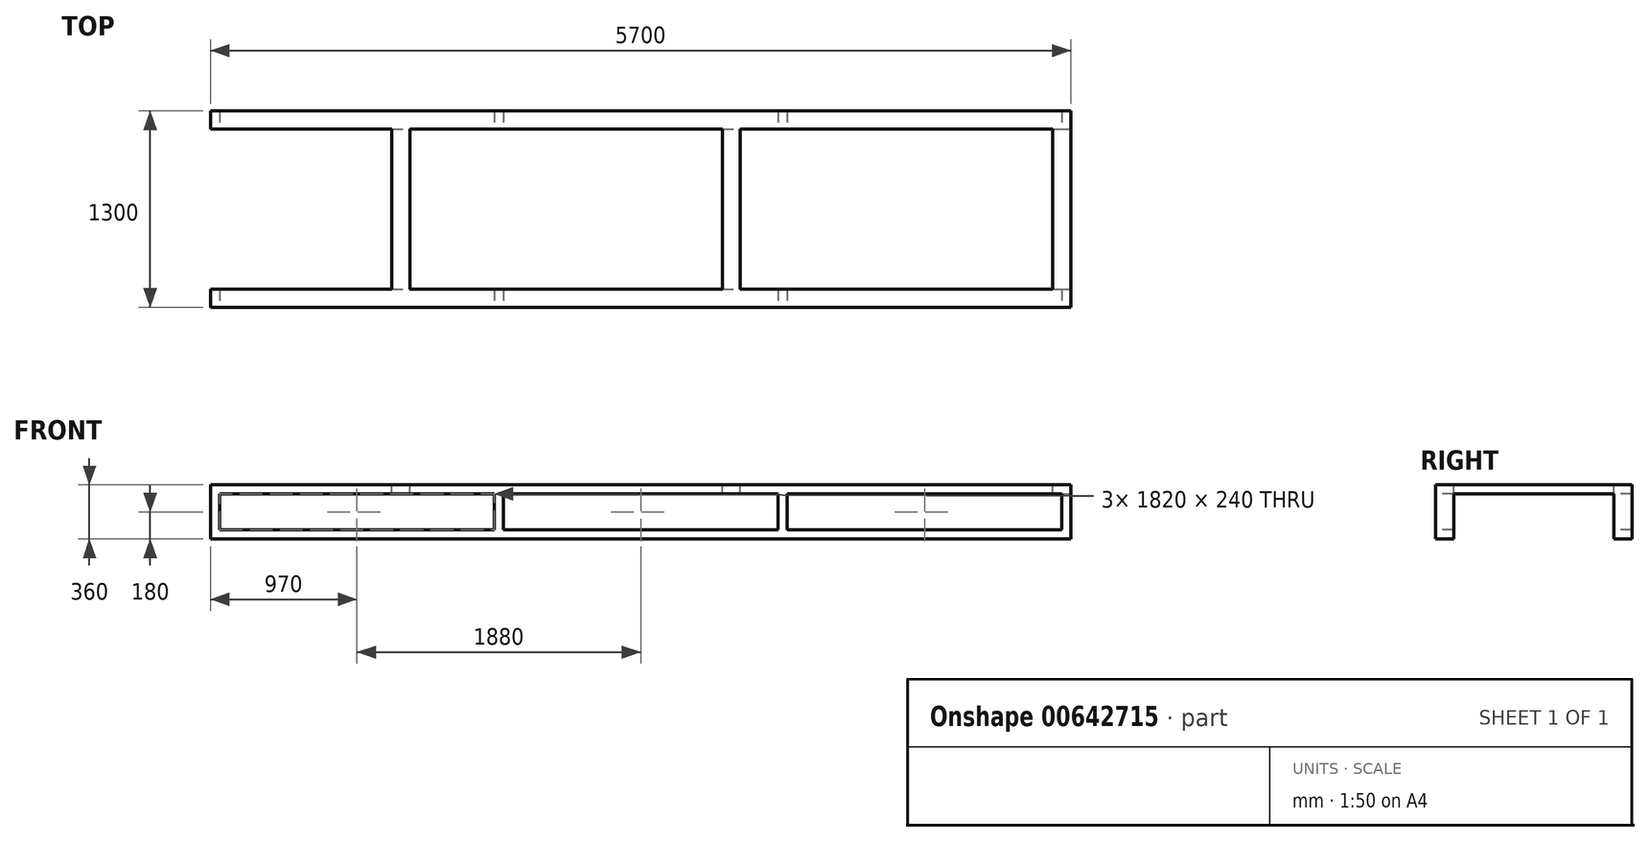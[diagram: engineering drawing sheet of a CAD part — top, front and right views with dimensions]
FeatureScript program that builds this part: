
annotation { "Feature Type Name" : "Feature", "Feature Type Description" : "" }
export const myFeature = defineFeature(function(context is Context, id is Id, definition is map)
    precondition{}
    {
        {
            var Q0;
            Q0=qCreatedBy(makeId("Top.planeOp"),FACE);
            var sketch = newSketch(context, id + "F0", { "sketchPlane" : qUnion([Q0])});
            skLineSegment(sketch, "E0.bottom", {"start": v(0, 0) * mm, "end": v(5700, 0) * mm});
            skLineSegment(sketch, "E0.top", {"start": v(0, 120) * mm, "end": v(5700, 120) * mm});
            skLineSegment(sketch, "E0.left", {"start": v(0, 0) * mm, "end": v(0, 120) * mm});
            skLineSegment(sketch, "E0.right", {"start": v(5700, 0) * mm, "end": v(5700, 120) * mm});
            skLineSegment(sketch, "E1.bottom", {"start": v(0, 1300) * mm, "end": v(5700, 1300) * mm});
            skLineSegment(sketch, "E1.top", {"start": v(0, 1180) * mm, "end": v(5700, 1180) * mm});
            skLineSegment(sketch, "E1.left", {"start": v(0, 1300) * mm, "end": v(0, 1180) * mm});
            skLineSegment(sketch, "E1.right", {"start": v(5700, 1300) * mm, "end": v(5700, 1180) * mm});
            skLineSegment(sketch, "E2.bottom", {"start": v(5700, 1180) * mm, "end": v(5580, 1180) * mm});
            skLineSegment(sketch, "E2.top", {"start": v(5700, 120) * mm, "end": v(5580, 120) * mm});
            skLineSegment(sketch, "E2.left", {"start": v(5700, 1180) * mm, "end": v(5700, 120) * mm});
            skLineSegment(sketch, "E2.right", {"start": v(5580, 1180) * mm, "end": v(5580, 120) * mm});
            skLineSegment(sketch, "E3.bottom", {"start": v(1200, 1180) * mm, "end": v(1320, 1180) * mm});
            skLineSegment(sketch, "E3.top", {"start": v(1200, 120) * mm, "end": v(1320, 120) * mm});
            skLineSegment(sketch, "E3.left", {"start": v(1200, 1180) * mm, "end": v(1200, 120) * mm});
            skLineSegment(sketch, "E3.right", {"start": v(1320, 1180) * mm, "end": v(1320, 120) * mm});
            skLineSegment(sketch, "E4.bottom", {"start": v(3390, 1180) * mm, "end": v(3510, 1180) * mm});
            skLineSegment(sketch, "E4.top", {"start": v(3390, 120) * mm, "end": v(3510, 120) * mm});
            skLineSegment(sketch, "E4.left", {"start": v(3390, 1180) * mm, "end": v(3390, 120) * mm});
            skLineSegment(sketch, "E4.right", {"start": v(3510, 1180) * mm, "end": v(3510, 120) * mm});
            skSolve(sketch);
        }
        {
            var Q0;
            Q0=makeQuery(id+"F0.imprint","IMPRINT",FACE,{"disambiguationData":[TD([[makeQuery(id+"F0.imprint","IMPRINT",EDGE,{"derivedFrom":sQuery(id+"F0.wireOp",EDGE,"E1.bottom")}),-1.0]])]});
            var Q1;
            Q1=makeQuery(id+"F0.imprint","IMPRINT",FACE,{"disambiguationData":[TD([[makeQuery(id+"F0.imprint","IMPRINT",EDGE,{"derivedFrom":sQuery(id+"F0.wireOp",EDGE,"E0.bottom")}),1.0]])]});
            var Q2;
            Q2=makeQuery(id+"F0.imprint","IMPRINT",FACE,{"disambiguationData":[TD([[makeQuery(id+"F0.imprint","IMPRINT",EDGE,{"derivedFrom":sQuery(id+"F0.wireOp",EDGE,"E3.bottom")}),-1.0]])]});
            var Q3;
            Q3=makeQuery(id+"F0.imprint","IMPRINT",FACE,{"disambiguationData":[TD([[makeQuery(id+"F0.imprint","IMPRINT",EDGE,{"derivedFrom":sQuery(id+"F0.wireOp",EDGE,"E4.bottom")}),-1.0]])]});
            var Q4;
            Q4=makeQuery(id+"F0.imprint","IMPRINT",FACE,{"disambiguationData":[TD([[makeQuery(id+"F0.imprint","IMPRINT",EDGE,{"derivedFrom":sQuery(id+"F0.wireOp",EDGE,"E2.bottom")}),1.0]])]});
            extrude(context, id + "F1", {"entities" : qUnion([Q0, Q1, Q2, Q3, Q4]), "depth" : 60 * mm, "offsetDistance" : 25 * mm});
        }
        {
            var Q0;
            Q0=makeQuery(id+"F1.opExtrude","CAP_FACE",FACE,{"disambiguationData":[OSD([sQuery(id+"F0.wireOp",EDGE,"E0.bottom"),sQuery(id+"F0.wireOp",EDGE,"E0.top"),sQuery(id+"F0.wireOp",EDGE,"E0.left"),sQuery(id+"F0.wireOp",EDGE,"E0.right"),sQuery(id+"F0.wireOp",EDGE,"E1.bottom"),sQuery(id+"F0.wireOp",EDGE,"E1.top"),sQuery(id+"F0.wireOp",EDGE,"E1.left"),sQuery(id+"F0.wireOp",EDGE,"E1.right"),sQuery(id+"F0.wireOp",EDGE,"E2.left"),sQuery(id+"F0.wireOp",EDGE,"E2.right"),sQuery(id+"F0.wireOp",EDGE,"E3.left"),sQuery(id+"F0.wireOp",EDGE,"E3.right"),sQuery(id+"F0.wireOp",EDGE,"E4.left"),sQuery(id+"F0.wireOp",EDGE,"E4.right")])],"isStart":false});
            var sketch = newSketch(context, id + "F2", { "sketchPlane" : qUnion([Q0])});
            skLineSegment(sketch, "E5.bottom", {"start": v(0, 1300) * mm, "end": v(60, 1300) * mm});
            skLineSegment(sketch, "E5.top", {"start": v(0, 1180) * mm, "end": v(60, 1180) * mm});
            skLineSegment(sketch, "E5.left", {"start": v(0, 1300) * mm, "end": v(0, 1180) * mm});
            skLineSegment(sketch, "E5.right", {"start": v(60, 1300) * mm, "end": v(60, 1180) * mm});
            skLineSegment(sketch, "E6.0.1.0", {"start": v(60, 120) * mm, "end": v(60, 0) * mm});
            skLineSegment(sketch, "E6.0.1.1", {"start": v(0, 0) * mm, "end": v(60, 0) * mm});
            skLineSegment(sketch, "E6.0.1.2", {"start": v(0, 120) * mm, "end": v(0, 0) * mm});
            skLineSegment(sketch, "E6.0.1.3", {"start": v(0, 120) * mm, "end": v(60, 120) * mm});
            skLineSegment(sketch, "E6.1.0.0", {"start": v(1940, 1300) * mm, "end": v(1940, 1180) * mm});
            skLineSegment(sketch, "E6.1.0.1", {"start": v(1880, 1180) * mm, "end": v(1940, 1180) * mm});
            skLineSegment(sketch, "E6.1.0.2", {"start": v(1880, 1300) * mm, "end": v(1880, 1180) * mm});
            skLineSegment(sketch, "E6.1.0.3", {"start": v(1880, 1300) * mm, "end": v(1940, 1300) * mm});
            skLineSegment(sketch, "E6.1.1.0", {"start": v(1940, 120) * mm, "end": v(1940, 0) * mm});
            skLineSegment(sketch, "E6.1.1.1", {"start": v(1880, 0) * mm, "end": v(1940, 0) * mm});
            skLineSegment(sketch, "E6.1.1.2", {"start": v(1880, 120) * mm, "end": v(1880, 0) * mm});
            skLineSegment(sketch, "E6.1.1.3", {"start": v(1880, 120) * mm, "end": v(1940, 120) * mm});
            skLineSegment(sketch, "E6.2.0.0", {"start": v(3820, 1300) * mm, "end": v(3820, 1180) * mm});
            skLineSegment(sketch, "E6.2.0.1", {"start": v(3760, 1180) * mm, "end": v(3820, 1180) * mm});
            skLineSegment(sketch, "E6.2.0.2", {"start": v(3760, 1300) * mm, "end": v(3760, 1180) * mm});
            skLineSegment(sketch, "E6.2.0.3", {"start": v(3760, 1300) * mm, "end": v(3820, 1300) * mm});
            skLineSegment(sketch, "E6.2.1.0", {"start": v(3820, 120) * mm, "end": v(3820, 0) * mm});
            skLineSegment(sketch, "E6.2.1.1", {"start": v(3760, 0) * mm, "end": v(3820, 0) * mm});
            skLineSegment(sketch, "E6.2.1.2", {"start": v(3760, 120) * mm, "end": v(3760, 0) * mm});
            skLineSegment(sketch, "E6.2.1.3", {"start": v(3760, 120) * mm, "end": v(3820, 120) * mm});
            skLineSegment(sketch, "E6.3.0.0", {"start": v(5700, 1300) * mm, "end": v(5700, 1180) * mm});
            skLineSegment(sketch, "E6.3.0.1", {"start": v(5640, 1180) * mm, "end": v(5700, 1180) * mm});
            skLineSegment(sketch, "E6.3.0.2", {"start": v(5640, 1300) * mm, "end": v(5640, 1180) * mm});
            skLineSegment(sketch, "E6.3.0.3", {"start": v(5640, 1300) * mm, "end": v(5700, 1300) * mm});
            skLineSegment(sketch, "E6.3.1.0", {"start": v(5700, 120) * mm, "end": v(5700, 0) * mm});
            skLineSegment(sketch, "E6.3.1.1", {"start": v(5640, 0) * mm, "end": v(5700, 0) * mm});
            skLineSegment(sketch, "E6.3.1.2", {"start": v(5640, 120) * mm, "end": v(5640, 0) * mm});
            skLineSegment(sketch, "E6.3.1.3", {"start": v(5640, 120) * mm, "end": v(5700, 120) * mm});
            skLineSegment(sketch, "E6.direction1", {"start": v(60, 1180) * mm, "end": v(1940, 1180) * mm, "construction": true});
            skLineSegment(sketch, "E6.direction2", {"start": v(60, 1180) * mm, "end": v(60, 0) * mm, "construction": true});
            skSolve(sketch);
        }
        {
            var Q0;
            Q0 = qSketchRegion(id + "F2", true);
            extrude(context, id + "F3", {"entities" : qUnion([Q0]), "operationType" : NewBodyOperationType.ADD, "depth" : 300 * mm, "offsetDistance" : 25 * mm});
        }
        {
            var Q0;
            Q0=makeQuery(id+"F3.opExtrude","CAP_FACE",FACE,{"disambiguationData":[OSD([sQuery(id+"F2.wireOp",EDGE,"E5.bottom"),sQuery(id+"F2.wireOp",EDGE,"E5.top"),sQuery(id+"F2.wireOp",EDGE,"E5.left"),sQuery(id+"F2.wireOp",EDGE,"E5.right")])],"isStart":false});
            var sketch = newSketch(context, id + "F4", { "sketchPlane" : qUnion([Q0])});
            skLineSegment(sketch, "E7.0", {"start": v(0, 1300) * mm, "end": v(0, 1180) * mm});
            skPoint(sketch, "E8.0", {"position": v(30, 1300) * mm});
            skLineSegment(sketch, "E9.0", {"start": v(0, 1300) * mm, "end": v(60, 1300) * mm});
            skLineSegment(sketch, "E10.0", {"start": v(0, 1180) * mm, "end": v(60, 1180) * mm});
            skPoint(sketch, "E11.0.end.orphan", {"position": v(1200, 1180) * mm});
            skPoint(sketch, "E11.0.start.orphan", {"position": v(60, 1180) * mm});
            skPoint(sketch, "E12.0.end.orphan", {"position": v(1880, 1300) * mm});
            skPoint(sketch, "E12.0.start.orphan", {"position": v(60, 1300) * mm});
            skPoint(sketch, "E13.0.end.orphan", {"position": v(1880, 1180) * mm});
            skPoint(sketch, "E13.0.start.orphan", {"position": v(1320, 1180) * mm});
            skPoint(sketch, "E14.0.end.orphan", {"position": v(1940, 1300) * mm});
            skLineSegment(sketch, "E15.0", {"start": v(0, 1300) * mm, "end": v(5700, 1300) * mm});
            skPoint(sketch, "E16.0", {"position": v(0, 1180) * mm});
            skLineSegment(sketch, "E17.0", {"start": v(0, 1180) * mm, "end": v(1200, 1180) * mm});
            skLineSegment(sketch, "E18.0", {"start": v(1320, 1180) * mm, "end": v(3390, 1180) * mm});
            skLineSegment(sketch, "E19.0", {"start": v(3510, 1180) * mm, "end": v(5580, 1180) * mm});
            skLineSegment(sketch, "E20.0", {"start": v(5700, 1300) * mm, "end": v(5700, 0) * mm});
            skLineSegment(sketch, "E21.0", {"start": v(0, 0) * mm, "end": v(5700, 0) * mm});
            skLineSegment(sketch, "E22.0", {"start": v(3510, 120) * mm, "end": v(5580, 120) * mm});
            skLineSegment(sketch, "E23.0", {"start": v(1320, 120) * mm, "end": v(3390, 120) * mm});
            skLineSegment(sketch, "E24.0", {"start": v(0, 120) * mm, "end": v(1200, 120) * mm});
            skLineSegment(sketch, "E25.0", {"start": v(0, 0) * mm, "end": v(0, 120) * mm});
            skLineSegment(sketch, "E26.0", {"start": v(5580, 1180) * mm, "end": v(5580, 120) * mm});
            skLineSegment(sketch, "E27", {"start": v(1200, 1180) * mm, "end": v(1320, 1180) * mm});
            skLineSegment(sketch, "E28", {"start": v(1200, 120) * mm, "end": v(1320, 120) * mm});
            skLineSegment(sketch, "E29", {"start": v(3390, 1180) * mm, "end": v(3510, 1180) * mm});
            skLineSegment(sketch, "E30", {"start": v(3390, 120) * mm, "end": v(3510, 120) * mm});
            skLineSegment(sketch, "E31.0", {"start": v(3390, 1180) * mm, "end": v(3390, 120) * mm});
            skLineSegment(sketch, "E32.0", {"start": v(3510, 1180) * mm, "end": v(3510, 120) * mm});
            skLineSegment(sketch, "E33.0", {"start": v(1320, 1180) * mm, "end": v(1320, 120) * mm});
            skLineSegment(sketch, "E34.0", {"start": v(1200, 1180) * mm, "end": v(1200, 120) * mm});
            skSolve(sketch);
        }
        {
            var Q0;
            Q0 = qSketchRegion(id + "F4", true);
            var Q1;
            Q1=makeQuery(id+"F4.imprint","IMPRINT",FACE,{"disambiguationData":[TD([[makeQuery(id+"F4.imprint","IMPRINT",EDGE,{"derivedFrom":sQuery(id+"F4.wireOp",EDGE,"E29")}),-1.0]])]});
            extrude(context, id + "F5", {"entities" : qUnion([Q0, Q1]), "operationType" : NewBodyOperationType.ADD, "oppositeDirection" : true, "depth" : 60 * mm, "offsetDistance" : 25 * mm});
        }
    });
